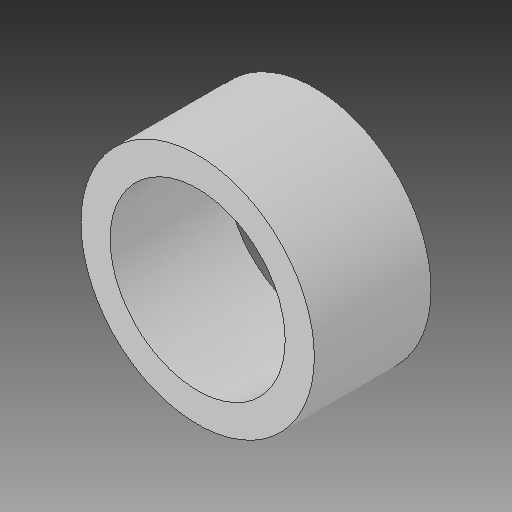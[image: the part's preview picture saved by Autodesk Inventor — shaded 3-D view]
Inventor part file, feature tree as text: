
AUTODESK INVENTOR PART (.ipt)
format: ipt  version: 2018 (Build 220112000, 112)  size: 92,672 bytes
history: native  units: in
note: dims shown in document units (in); Inventor stores cm internally (conversion verified against a paired STEP export)
features: revolve x1
ambient origin geometry x8: Origin, YZ Plane, XZ Plane, XY Plane, X Axis, Y Axis, Z Axis, Center Point
bodies: Solid1 (feature_tree)
feature tree (1):
  revolve  "Revolve1"  [1 undecoded]
note: 1 required parameter value undecoded (feature->parameter linkage not recoverable at this tier; creation-order binding heuristic only, values carry confidence <= 0.55)
